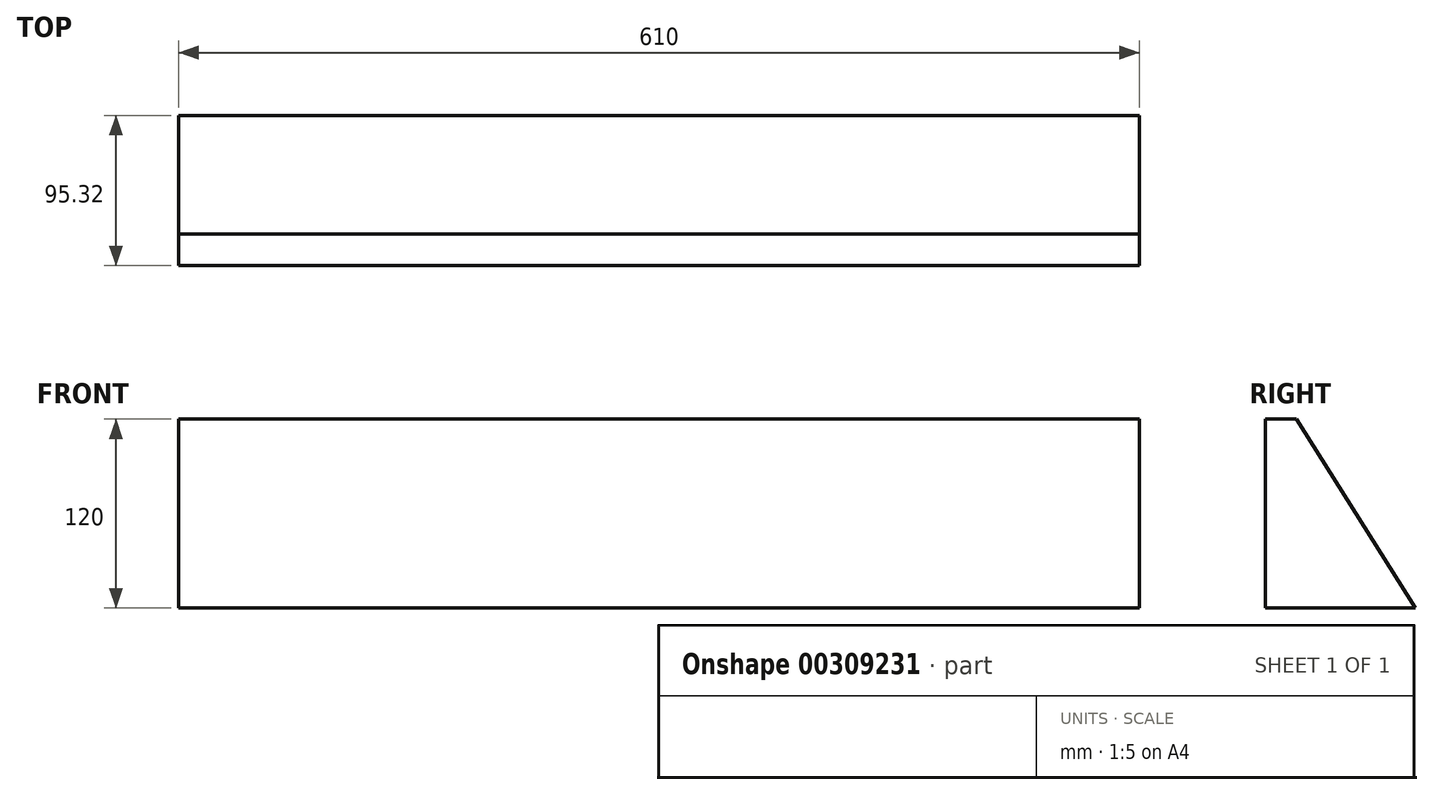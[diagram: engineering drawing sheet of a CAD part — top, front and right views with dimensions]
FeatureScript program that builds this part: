
annotation { "Feature Type Name" : "Feature", "Feature Type Description" : "" }
export const myFeature = defineFeature(function(context is Context, id is Id, definition is map)
    precondition{}
    {
        {
            var Q0;
            Q0=qCreatedBy(makeId("Right.planeOp"),FACE);
            var sketch = newSketch(context, id + "F0", { "sketchPlane" : qUnion([Q0])});
            skLineSegment(sketch, "E0.bottom", {"start": v(0, 0) * mm, "end": v(95.32, 0) * mm});
            skLineSegment(sketch, "E0.top", {"start": v(0, 120) * mm, "end": v(19.9, 120) * mm});
            skLineSegment(sketch, "E0.left", {"start": v(0, 0) * mm, "end": v(0, 120) * mm});
            skLineSegment(sketch, "E1", {"start": v(19.9, 120) * mm, "end": v(95.32, 0) * mm});
            skSolve(sketch);
        }
        {
            var Q0;
            Q0=makeQuery(id+"F0.imprint","IMPRINT",FACE,{"disambiguationData":[TD([[makeQuery(id+"F0.imprint","IMPRINT",EDGE,{"derivedFrom":sQuery(id+"F0.wireOp",EDGE,"E0.bottom")}),1.0]])]});
            extrude(context, id + "F1", {"entities" : qUnion([Q0]), "oppositeDirection" : true, "depth" : 610 * mm});
        }
    });
